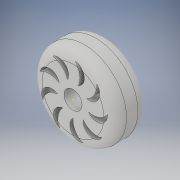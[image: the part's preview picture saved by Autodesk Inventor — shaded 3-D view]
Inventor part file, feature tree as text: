
AUTODESK INVENTOR PART (.ipt)
format: ipt  version: 2019 (Build 230136000, 136)  size: 510,464 bytes
history: native  units: mm
features: sketch x4, extrude x3, other x1, pattern_circular x1, fillet x1
ambient origin geometry x8: Origin, YZ Plane, XZ Plane, XY Plane, X Axis, Y Axis, Z Axis, Center Point
bodies: Body1 (feature_tree), Body2 (feature_tree), Body3 (feature_tree)
feature tree (10):
  other  "Bryła1"
  extrude  "Wyciągnięcie proste1"  Depth=14.9mm
  extrude  "Wyciągnięcie proste2"  Depth=6.0mm TaperAngle=0.0deg
  sketch  "Szkic3"
  extrude  "Wyciągnięcie proste3"  Depth=3.2mm
  pattern_circular  "Szyk kołowy1"  [2 undecoded]
  fillet  "Zaokrąglenie1"  Radius=3.45mm
  sketch  "Szkic1"
  sketch  "Szkic2"
  sketch  "Szkic4"
note: 2 required parameter values undecoded (feature->parameter linkage not recoverable at this tier; creation-order binding heuristic only, values carry confidence <= 0.55)
